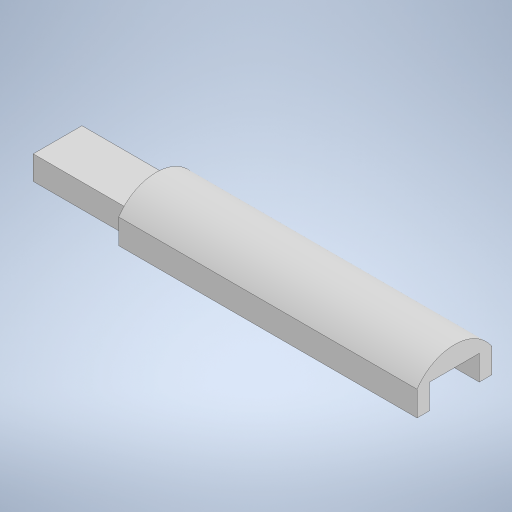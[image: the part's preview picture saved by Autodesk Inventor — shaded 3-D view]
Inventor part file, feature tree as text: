
AUTODESK INVENTOR PART (.ipt)
format: ipt  version: 2023 (Build 270158000, 158)  size: 265,728 bytes
history: native  units: in
note: dims shown in document units (in); Inventor stores cm internally (conversion verified against a paired STEP export)
features: extrude x4, sketch x4, projected_geometry x3
ambient origin geometry x8: Origin, YZ Plane, XZ Plane, XY Plane, X Axis, Y Axis, Z Axis, Center Point
bodies: Solid1 (feature_tree)
feature tree (11):
  extrude  "Extrusion1"  Depth=0.75in
  extrude  "Extrusion2"  Depth=1.5in
  extrude  "Extrusion3"  Depth=0.49in
  extrude  "Extrusion4"  Depth=0.25in TaperAngle=0.0deg
  sketch  "Sketch1"  dims[d0=3.0in d1=0.75in]
  sketch  "Sketch2"  dims[d2=0.375in d3=1.5in]
  projected_geometry  "Projected Loop1"
  sketch  "Sketch3"  dims[d4=0.99in d5=0.49in]
  projected_geometry  "Projected Loop2"
  sketch  "Sketch4"  dims[d6=0.245in d7=0.25in d8=0.0in d9=3.0in d10=0.0in d11=0.5in d12=0.49in d13=0.25in d14=1.0in d15=0.25in d16=0.0in d17=0.01in d18=0.0in]
  projected_geometry  "Projected Loop3"
